# Revit family: Hager-UNIVERS-Hollow_wall-IP30-With_Cover-With_DIN-NoHosted-DE-de
name_source: partatom
category: Electrical Equipment
units: mm (PartAtom-declared; Revit-internal decimal feet)

## family parameters
Always vertical = Yes
Cut with Voids When Loaded = No
Maintain Annotation Orientation = No
Panel Configuration = Two Columns, Circuits Across
Part Type = Panelboard
Room Calculation Point = No
Round Connector Dimension = Use Diameter
Shared = No
Work Plane-Based = Yes

## types (28) — shared parameters
Code hager = ADD-EC000214_EU
Default Elevation = 1200 mm
EF000003 - Montageart = Hohlwand
EF000007 - Farbe = weiß
EF000024 - UV-beständig = No
EF000049 - Tiefe = 125 mm  [stored 0.410105 ft]
EF000116 - RAL-Nummer = 9010
EF000118 - Mit Montageplatte = No
EF000218 - Einbautiefe = 112 mm  [stored 0.367454 ft]
EF001062 - EMV-Ausführung = No
EF001088 - Anbaumöglichkeit = Yes
EF001134 - DIN-Schiene = Yes
EF002950 - Breite in Teilungseinheiten = 12
EF004462 - Art der Schließung = sonstige
EF005474 - Schutzart (IP) = IP30
EF006244 - Transparenter Deckel/Tür = No
EF006306 - Mit Schloss = No
EF015941 - Signaldurchlassende Tür = No
ETIM class code = EC000214
ETIM class name = Small distribution board
HG000002-Mit tür = Yes
HG000003-Bereich = UNIVERS
HG000005-Dicke = 2 mm  [stored 0.00656168 ft]
HG000006-Flush mounted = Yes
HG000011-Leere Reihen von unten = No
HG000012-Türschwenkwinkel = 90.00°
HG000013-Tür links = No
HG000014-Tür rechts = Yes
HG000015-Sichtbarkeit der Türöffnung = Yes
HG000016-3D-Türsichtbarkeit = Yes
HG000017-Distanz zwischen den Polen = 18 mm  [stored 0.0590551 ft]
HG000060-RAL-number = 9010
HG000099-Onfly Template ID-de-DE = 507532
HGEF0002950-Breite in Teilungseinheiten = 12
Manufacturer = Hager
Name BIM&CO = Electricity
Name hager = ADD_Enclosures_EC000214
Reference = Template-Enclosure_EU-EC000214
Uniformat = Low Tension Service & Dist.
Uniformat code = D501001
zero-valued in all types: EF001131 - Innentiefe, HG000007-Anzahl der leeren Spalten, HG000008-Anzahl der leeren Reihen

## per-type parameters (varying)
| type | BC_METADATA | EF000008 - Breite | EF000040 - Höhe | EF000266 - Anzahl der Reihen | EF000332 - Einbauhöhe | EF000846 - Einbaubreite | EF009212 - Ausführung Deckel | EF015776 - Erdungsklemmenblock | EF015777 - Neutralleiterklemmenblock | HG000001-Anzahl der Spalten | HG000004-Herstellerreferenz | HG000009-Doppelflügeligen Tür | HG000010-Asymmetrische Türen | HGEF000266-Anzahl der Reihen |
| UNIVERS-Hollow_wall_W353_H553_D125_12_Modular_Spacing-FWU31A | {"ObjectGuid":"004b6e42-337b-4bcf-8371-5aba0abf1001","ModelGuid":"c4caa68d-46ce-4c8b-a1d1-fddb7e9099eb","VariantGuid":"0e4282af-3eaf-429b-9620-5d72cca2878c","Revision":"#6","VariantName":"UNIVERS-Hollow_wall_W353_H553_D125_12_Modular_Spacing-FWU31A"} | 353 mm  [stored 1.15814 ft] | 553 mm  [stored 1.8143 ft] | 3 | 502 mm  [stored 1.64698 ft] | 310 mm  [stored 1.01706 ft] | geschlossen | No | No | 1 | FWU31A | No | No | 3 |
| UNIVERS-Hollow_wall_W353_H553_D125_12_Modular_Spacing-FWU31S | {"ObjectGuid":"004b6e42-337b-4bcf-8371-5aba0abf1001","ModelGuid":"c4caa68d-46ce-4c8b-a1d1-fddb7e9099eb","VariantGuid":"141f29b6-52fd-4358-8fc3-3b4451ea5a45","Revision":"#6","VariantName":"UNIVERS-Hollow_wall_W353_H553_D125_12_Modular_Spacing-FWU31S"} | 353 mm  [stored 1.15814 ft] | 553 mm  [stored 1.8143 ft] | 3 | 502 mm  [stored 1.64698 ft] | 310 mm  [stored 1.01706 ft] | mit Ausschnitt | Yes | Yes | 1 | FWU31S | No | No | 3 |
| UNIVERS-Hollow_wall_W603_H553_D125_12_Modular_Spacing-FWU32A | {"ObjectGuid":"004b6e42-337b-4bcf-8371-5aba0abf1001","ModelGuid":"c4caa68d-46ce-4c8b-a1d1-fddb7e9099eb","VariantGuid":"bc327333-84a1-4712-8c00-3abd35c20ae2","Revision":"#6","VariantName":"UNIVERS-Hollow_wall_W603_H553_D125_12_Modular_Spacing-FWU32A"} | 603 mm | 553 mm  [stored 1.8143 ft] | 3 | 502 mm  [stored 1.64698 ft] | 560 mm  [stored 1.83727 ft] | geschlossen | No | No | 2 | FWU32A | No | No | 3 |
| UNIVERS-Hollow_wall_W603_H553_D125_12_Modular_Spacing-FWU32S | {"ObjectGuid":"004b6e42-337b-4bcf-8371-5aba0abf1001","ModelGuid":"c4caa68d-46ce-4c8b-a1d1-fddb7e9099eb","VariantGuid":"0b09216e-6169-455d-aa72-aab511c9882a","Revision":"#6","VariantName":"UNIVERS-Hollow_wall_W603_H553_D125_12_Modular_Spacing-FWU32S"} | 603 mm | 553 mm  [stored 1.8143 ft] | 3 | 502 mm  [stored 1.64698 ft] | 560 mm  [stored 1.83727 ft] | mit Ausschnitt | Yes | No | 2 | FWU32S | No | No | 3 |
| UNIVERS-Hollow_wall_W853_H553_D125_12_Modular_Spacing-FWU33A | {"ObjectGuid":"004b6e42-337b-4bcf-8371-5aba0abf1001","ModelGuid":"c4caa68d-46ce-4c8b-a1d1-fddb7e9099eb","VariantGuid":"f21cd202-9285-4477-bfae-d84053fc58a3","Revision":"#6","VariantName":"UNIVERS-Hollow_wall_W853_H553_D125_12_Modular_Spacing-FWU33A"} | 853 mm  [stored 2.79856 ft] | 553 mm  [stored 1.8143 ft] | 3 | 502 mm  [stored 1.64698 ft] | 810 mm | geschlossen | No | No | 3 | FWU33A | Yes | Yes | 3 |
| UNIVERS-Hollow_wall_W853_H553_D125_12_Modular_Spacing-FWU33S | {"ObjectGuid":"004b6e42-337b-4bcf-8371-5aba0abf1001","ModelGuid":"c4caa68d-46ce-4c8b-a1d1-fddb7e9099eb","VariantGuid":"6b30a440-94ab-4b75-991e-5ca1c1a31157","Revision":"#6","VariantName":"UNIVERS-Hollow_wall_W853_H553_D125_12_Modular_Spacing-FWU33S"} | 853 mm  [stored 2.79856 ft] | 553 mm  [stored 1.8143 ft] | 3 | 502 mm  [stored 1.64698 ft] | 810 mm | mit Ausschnitt | Yes | No | 3 | FWU33S | Yes | Yes | 3 |
| UNIVERS-Hollow_wall_W353_H703_D125_12_Modular_Spacing-FWU41A | {"ObjectGuid":"004b6e42-337b-4bcf-8371-5aba0abf1001","ModelGuid":"c4caa68d-46ce-4c8b-a1d1-fddb7e9099eb","VariantGuid":"74a8f86c-bf76-4138-8333-80e0311d3bd7","Revision":"#6","VariantName":"UNIVERS-Hollow_wall_W353_H703_D125_12_Modular_Spacing-FWU41A"} | 353 mm  [stored 1.15814 ft] | 703 mm  [stored 2.30643 ft] | 4 | 652 mm  [stored 2.13911 ft] | 310 mm  [stored 1.01706 ft] | geschlossen | No | No | 1 | FWU41A | No | No | 4 |
| UNIVERS-Hollow_wall_W353_H703_D125_12_Modular_Spacing-FWU41S | {"ObjectGuid":"004b6e42-337b-4bcf-8371-5aba0abf1001","ModelGuid":"c4caa68d-46ce-4c8b-a1d1-fddb7e9099eb","VariantGuid":"c0dc75cd-428a-403a-953f-171c5bfc0ae7","Revision":"#6","VariantName":"UNIVERS-Hollow_wall_W353_H703_D125_12_Modular_Spacing-FWU41S"} | 353 mm  [stored 1.15814 ft] | 703 mm  [stored 2.30643 ft] | 4 | 652 mm  [stored 2.13911 ft] | 310 mm  [stored 1.01706 ft] | mit Ausschnitt | Yes | No | 1 | FWU41S | No | No | 4 |
| UNIVERS-Hollow_wall_W603_H703_D125_12_Modular_Spacing-FWU42A | {"ObjectGuid":"004b6e42-337b-4bcf-8371-5aba0abf1001","ModelGuid":"c4caa68d-46ce-4c8b-a1d1-fddb7e9099eb","VariantGuid":"f52d9ca4-0408-490c-9202-22d2f044d4a7","Revision":"#6","VariantName":"UNIVERS-Hollow_wall_W603_H703_D125_12_Modular_Spacing-FWU42A"} | 603 mm | 703 mm  [stored 2.30643 ft] | 4 | 652 mm  [stored 2.13911 ft] | 560 mm  [stored 1.83727 ft] | geschlossen | No | No | 2 | FWU42A | No | No | 4 |
| UNIVERS-Hollow_wall_W603_H703_D125_12_Modular_Spacing-FWU42S | {"ObjectGuid":"004b6e42-337b-4bcf-8371-5aba0abf1001","ModelGuid":"c4caa68d-46ce-4c8b-a1d1-fddb7e9099eb","VariantGuid":"750bc919-138d-4591-95ea-020844d4682a","Revision":"#6","VariantName":"UNIVERS-Hollow_wall_W603_H703_D125_12_Modular_Spacing-FWU42S"} | 603 mm | 703 mm  [stored 2.30643 ft] | 4 | 652 mm  [stored 2.13911 ft] | 560 mm  [stored 1.83727 ft] | mit Ausschnitt | Yes | No | 2 | FWU42S | No | No | 4 |
| UNIVERS-Hollow_wall_W853_H703_D125_12_Modular_Spacing-FWU43A | {"ObjectGuid":"004b6e42-337b-4bcf-8371-5aba0abf1001","ModelGuid":"c4caa68d-46ce-4c8b-a1d1-fddb7e9099eb","VariantGuid":"f4954e4e-cce7-426a-bee3-867e0bb60f88","Revision":"#6","VariantName":"UNIVERS-Hollow_wall_W853_H703_D125_12_Modular_Spacing-FWU43A"} | 853 mm  [stored 2.79856 ft] | 703 mm  [stored 2.30643 ft] | 4 | 652 mm  [stored 2.13911 ft] | 810 mm | geschlossen | No | No | 3 | FWU43A | Yes | Yes | 4 |
| UNIVERS-Hollow_wall_W853_H703_D125_12_Modular_Spacing-FWU43S | {"ObjectGuid":"004b6e42-337b-4bcf-8371-5aba0abf1001","ModelGuid":"c4caa68d-46ce-4c8b-a1d1-fddb7e9099eb","VariantGuid":"8960139d-813b-48f6-b8c3-3bac7f311ae3","Revision":"#6","VariantName":"UNIVERS-Hollow_wall_W853_H703_D125_12_Modular_Spacing-FWU43S"} | 853 mm  [stored 2.79856 ft] | 703 mm  [stored 2.30643 ft] | 4 | 652 mm  [stored 2.13911 ft] | 810 mm | mit Ausschnitt | Yes | No | 3 | FWU43S | Yes | Yes | 4 |
| UNIVERS-Hollow_wall_W353_H853_D125_12_Modular_Spacing-FWU51A | {"ObjectGuid":"004b6e42-337b-4bcf-8371-5aba0abf1001","ModelGuid":"c4caa68d-46ce-4c8b-a1d1-fddb7e9099eb","VariantGuid":"2f7189d4-b223-4eca-b540-e5796fbe98a8","Revision":"#6","VariantName":"UNIVERS-Hollow_wall_W353_H853_D125_12_Modular_Spacing-FWU51A"} | 353 mm  [stored 1.15814 ft] | 853 mm  [stored 2.79856 ft] | 5 | 802 mm  [stored 2.63123 ft] | 310 mm  [stored 1.01706 ft] | geschlossen | No | No | 1 | FWU51A | No | No | 5 |
| UNIVERS-Hollow_wall_W353_H853_D125_12_Modular_Spacing-FWU51S | {"ObjectGuid":"004b6e42-337b-4bcf-8371-5aba0abf1001","ModelGuid":"c4caa68d-46ce-4c8b-a1d1-fddb7e9099eb","VariantGuid":"c47167d5-dd27-458c-ac27-afa67423d455","Revision":"#6","VariantName":"UNIVERS-Hollow_wall_W353_H853_D125_12_Modular_Spacing-FWU51S"} | 353 mm  [stored 1.15814 ft] | 853 mm  [stored 2.79856 ft] | 5 | 802 mm  [stored 2.63123 ft] | 310 mm  [stored 1.01706 ft] | mit Ausschnitt | Yes | No | 1 | FWU51S | No | No | 5 |
| UNIVERS-Hollow_wall_W603_H853_D125_12_Modular_Spacing-FWU52A | {"ObjectGuid":"004b6e42-337b-4bcf-8371-5aba0abf1001","ModelGuid":"c4caa68d-46ce-4c8b-a1d1-fddb7e9099eb","VariantGuid":"5cb0f389-1f31-48fd-9f50-e7bb2846f9c2","Revision":"#6","VariantName":"UNIVERS-Hollow_wall_W603_H853_D125_12_Modular_Spacing-FWU52A"} | 603 mm | 853 mm  [stored 2.79856 ft] | 5 | 802 mm  [stored 2.63123 ft] | 560 mm  [stored 1.83727 ft] | geschlossen | No | No | 2 | FWU52A | No | No | 5 |
| UNIVERS-Hollow_wall_W603_H853_D125_12_Modular_Spacing-FWU52S | {"ObjectGuid":"004b6e42-337b-4bcf-8371-5aba0abf1001","ModelGuid":"c4caa68d-46ce-4c8b-a1d1-fddb7e9099eb","VariantGuid":"54b6e612-c8f3-4439-887b-b5aafdb037a5","Revision":"#6","VariantName":"UNIVERS-Hollow_wall_W603_H853_D125_12_Modular_Spacing-FWU52S"} | 603 mm | 853 mm  [stored 2.79856 ft] | 5 | 802 mm  [stored 2.63123 ft] | 560 mm  [stored 1.83727 ft] | mit Ausschnitt | Yes | No | 2 | FWU52S | No | No | 5 |
| UNIVERS-Hollow_wall_W353_H1003_D125_12_Modular_Spacing-FWU61A | {"ObjectGuid":"004b6e42-337b-4bcf-8371-5aba0abf1001","ModelGuid":"c4caa68d-46ce-4c8b-a1d1-fddb7e9099eb","VariantGuid":"809823ed-e84b-4d28-9756-89b47f6e261e","Revision":"#6","VariantName":"UNIVERS-Hollow_wall_W353_H1003_D125_12_Modular_Spacing-FWU61A"} | 353 mm  [stored 1.15814 ft] | 1003 mm  [stored 3.29068 ft] | 6 | 952 mm  [stored 3.12336 ft] | 310 mm  [stored 1.01706 ft] | geschlossen | No | No | 1 | FWU61A | No | No | 6 |
| UNIVERS-Hollow_wall_W353_H1003_D125_12_Modular_Spacing-FWU61S | {"ObjectGuid":"004b6e42-337b-4bcf-8371-5aba0abf1001","ModelGuid":"c4caa68d-46ce-4c8b-a1d1-fddb7e9099eb","VariantGuid":"ed278378-abef-44f0-a442-52256c3047ad","Revision":"#6","VariantName":"UNIVERS-Hollow_wall_W353_H1003_D125_12_Modular_Spacing-FWU61S"} | 353 mm  [stored 1.15814 ft] | 1003 mm  [stored 3.29068 ft] | 6 | 952 mm  [stored 3.12336 ft] | 310 mm  [stored 1.01706 ft] | mit Ausschnitt | Yes | No | 1 | FWU61S | No | No | 6 |
| UNIVERS-Hollow_wall_W603_H1003_D125_12_Modular_Spacing-FWU62A | {"ObjectGuid":"004b6e42-337b-4bcf-8371-5aba0abf1001","ModelGuid":"c4caa68d-46ce-4c8b-a1d1-fddb7e9099eb","VariantGuid":"151638ea-4e1c-4229-a62a-df40f0e38b71","Revision":"#6","VariantName":"UNIVERS-Hollow_wall_W603_H1003_D125_12_Modular_Spacing-FWU62A"} | 603 mm | 1003 mm  [stored 3.29068 ft] | 6 | 952 mm  [stored 3.12336 ft] | 560 mm  [stored 1.83727 ft] | geschlossen | No | No | 2 | FWU62A | No | No | 6 |
| UNIVERS-Hollow_wall_W603_H1003_D125_12_Modular_Spacing-FWU62S | {"ObjectGuid":"004b6e42-337b-4bcf-8371-5aba0abf1001","ModelGuid":"c4caa68d-46ce-4c8b-a1d1-fddb7e9099eb","VariantGuid":"87313022-2381-4a66-a301-9f73cbd4b893","Revision":"#6","VariantName":"UNIVERS-Hollow_wall_W603_H1003_D125_12_Modular_Spacing-FWU62S"} | 603 mm | 1003 mm  [stored 3.29068 ft] | 6 | 952 mm  [stored 3.12336 ft] | 560 mm  [stored 1.83727 ft] | mit Ausschnitt | Yes | No | 2 | FWU62S | No | No | 6 |
| UNIVERS-Hollow_wall_W853_H1003_D125_12_Modular_Spacing-FWU63A | {"ObjectGuid":"004b6e42-337b-4bcf-8371-5aba0abf1001","ModelGuid":"c4caa68d-46ce-4c8b-a1d1-fddb7e9099eb","VariantGuid":"a70f0653-fbeb-4204-a6db-2c53a94370a1","Revision":"#6","VariantName":"UNIVERS-Hollow_wall_W853_H1003_D125_12_Modular_Spacing-FWU63A"} | 853 mm  [stored 2.79856 ft] | 1003 mm  [stored 3.29068 ft] | 6 | 952 mm  [stored 3.12336 ft] | 810 mm | geschlossen | No | No | 3 | FWU63A | Yes | Yes | 6 |
| UNIVERS-Hollow_wall_W853_H1003_D125_12_Modular_Spacing-FWU63S | {"ObjectGuid":"004b6e42-337b-4bcf-8371-5aba0abf1001","ModelGuid":"c4caa68d-46ce-4c8b-a1d1-fddb7e9099eb","VariantGuid":"6914eddb-2313-4a1a-aecf-77405d960523","Revision":"#6","VariantName":"UNIVERS-Hollow_wall_W853_H1003_D125_12_Modular_Spacing-FWU63S"} | 853 mm  [stored 2.79856 ft] | 1003 mm  [stored 3.29068 ft] | 6 | 952 mm  [stored 3.12336 ft] | 810 mm | mit Ausschnitt | Yes | No | 3 | FWU63S | Yes | Yes | 6 |
| UNIVERS-Hollow_wall_W353_H1153_D125_12_Modular_Spacing-FWU71A | {"ObjectGuid":"004b6e42-337b-4bcf-8371-5aba0abf1001","ModelGuid":"c4caa68d-46ce-4c8b-a1d1-fddb7e9099eb","VariantGuid":"38ced062-6fec-4c2a-8f8d-b35bd1461376","Revision":"#6","VariantName":"UNIVERS-Hollow_wall_W353_H1153_D125_12_Modular_Spacing-FWU71A"} | 353 mm  [stored 1.15814 ft] | 1153 mm | 7 | 1102 mm  [stored 3.61549 ft] | 310 mm  [stored 1.01706 ft] | geschlossen | No | No | 1 | FWU71A | No | No | 7 |
| UNIVERS-Hollow_wall_W353_H1153_D125_12_Modular_Spacing-FWU71S | {"ObjectGuid":"004b6e42-337b-4bcf-8371-5aba0abf1001","ModelGuid":"c4caa68d-46ce-4c8b-a1d1-fddb7e9099eb","VariantGuid":"60acbc5a-f172-43d8-9d43-6592bbe206c7","Revision":"#6","VariantName":"UNIVERS-Hollow_wall_W353_H1153_D125_12_Modular_Spacing-FWU71S"} | 353 mm  [stored 1.15814 ft] | 1153 mm | 7 | 1102 mm  [stored 3.61549 ft] | 310 mm  [stored 1.01706 ft] | mit Ausschnitt | Yes | No | 1 | FWU71S | No | No | 7 |
| UNIVERS-Hollow_wall_W603_H1153_D125_12_Modular_Spacing-FWU72A | {"ObjectGuid":"004b6e42-337b-4bcf-8371-5aba0abf1001","ModelGuid":"c4caa68d-46ce-4c8b-a1d1-fddb7e9099eb","VariantGuid":"fc0d92e6-ee8b-42cc-b756-7d6c652e9f22","Revision":"#6","VariantName":"UNIVERS-Hollow_wall_W603_H1153_D125_12_Modular_Spacing-FWU72A"} | 603 mm | 1153 mm | 7 | 1102 mm  [stored 3.61549 ft] | 560 mm  [stored 1.83727 ft] | geschlossen | No | No | 2 | FWU72A | No | No | 7 |
| UNIVERS-Hollow_wall_W603_H1153_D125_12_Modular_Spacing-FWU72S | {"ObjectGuid":"004b6e42-337b-4bcf-8371-5aba0abf1001","ModelGuid":"c4caa68d-46ce-4c8b-a1d1-fddb7e9099eb","VariantGuid":"087096f6-3455-4942-bcab-ecae702a0c67","Revision":"#6","VariantName":"UNIVERS-Hollow_wall_W603_H1153_D125_12_Modular_Spacing-FWU72S"} | 603 mm | 1153 mm | 7 | 1102 mm  [stored 3.61549 ft] | 560 mm  [stored 1.83727 ft] | mit Ausschnitt | Yes | No | 2 | FWU72S | No | No | 7 |
| UNIVERS-Hollow_wall_W853_H1153_D125_12_Modular_Spacing-FWU73A | {"ObjectGuid":"004b6e42-337b-4bcf-8371-5aba0abf1001","ModelGuid":"c4caa68d-46ce-4c8b-a1d1-fddb7e9099eb","VariantGuid":"9afd2258-1976-48d7-9a02-e98692895dbd","Revision":"#6","VariantName":"UNIVERS-Hollow_wall_W853_H1153_D125_12_Modular_Spacing-FWU73A"} | 853 mm  [stored 2.79856 ft] | 1153 mm | 7 | 1102 mm  [stored 3.61549 ft] | 810 mm | geschlossen | No | No | 3 | FWU73A | Yes | Yes | 7 |
| UNIVERS-Hollow_wall_W853_H1153_D125_12_Modular_Spacing-FWU73S | {"ObjectGuid":"004b6e42-337b-4bcf-8371-5aba0abf1001","ModelGuid":"c4caa68d-46ce-4c8b-a1d1-fddb7e9099eb","VariantGuid":"5cfdae0c-ce9f-4f57-84e9-c0dbd003b492","Revision":"#6","VariantName":"UNIVERS-Hollow_wall_W853_H1153_D125_12_Modular_Spacing-FWU73S"} | 853 mm  [stored 2.79856 ft] | 1153 mm | 7 | 1102 mm  [stored 3.61549 ft] | 810 mm | mit Ausschnitt | Yes | Yes | 3 | FWU73S | Yes | Yes | 7 |

note: [stored X ft] marks values corroborated as IEEE doubles in the binary element streams (Revit-internal decimal feet)

## geometry (parser evidence)
native form markers: Sweep x17
no freeform markers — native parametric forms only
